# Revit family: In-Line-Centrifugal-Duct-Fan_VIDK_Carnes
name_source: partatom
category: Mechanical Equipment
revit_build: Autodesk Revit Architecture 2012 (Build: 20110916_2132(x64)
units: mm (PartAtom-declared; Revit-internal decimal feet)

## types (6) — shared parameters
04 CSI = 23 34 23
95 CSI = 15830
Assembly Code = D3040200
Catalog URL = http://www.carnes.com
Description = Centrifugal Duct Fan
Housing = Aluminum-Carnes-Spun-Brushed
IOM Instructions URL = http://www.carnes.com
Manufacturer = Carnes Company
Manufacturer Fax = 608-845-6470
Product Page URL = http://www.carnes.com
URL = http://www.carnes.com
Warranty URL = http://www.carnes.com
ecoScorecard Product Page = http://ecoscorecard.com
zero-valued in all types: Default Elevation

## per-type parameters (varying)
| type | A | B | C | D | Damper Size | E | F | Radius |
| VIDK 06 | 14 " | 28.625 " | 12 " | 16.5 " | 12 " | 25.125 " | 12.5 " | 6 " |
| VIDK 08 | 14 " | 28.625 " | 12 " | 16.5 " | 12 " | 25.125 " | 12.5 " | 6 " |
| VIDK 10 | 18 " | 32.125 " | 16 " | 20.5 " | 16 " | 28.625 " | 16.5 " | 8 " |
| VIDK 12 | 18 " | 32.125 " | 16 " | 20.5 " | 16 " | 28.625 " | 16.5 " | 8 " |
| VIDK 15 | 24 " | 34.875 " | 22 " | 26.5 " | 22 " | 31.375 " | 22.5 " | 11 " |
| VIDK 18 | 28 " | 36.125 " | 26 " | 30.5 " | 26 " | 32.625 " | 26.5 " | 13 " |

note: column(s) folded — value = type name in every type: Model

## geometry (parser evidence)
native form markers: Blend x4, Sweep x3
no freeform markers — native parametric forms only
